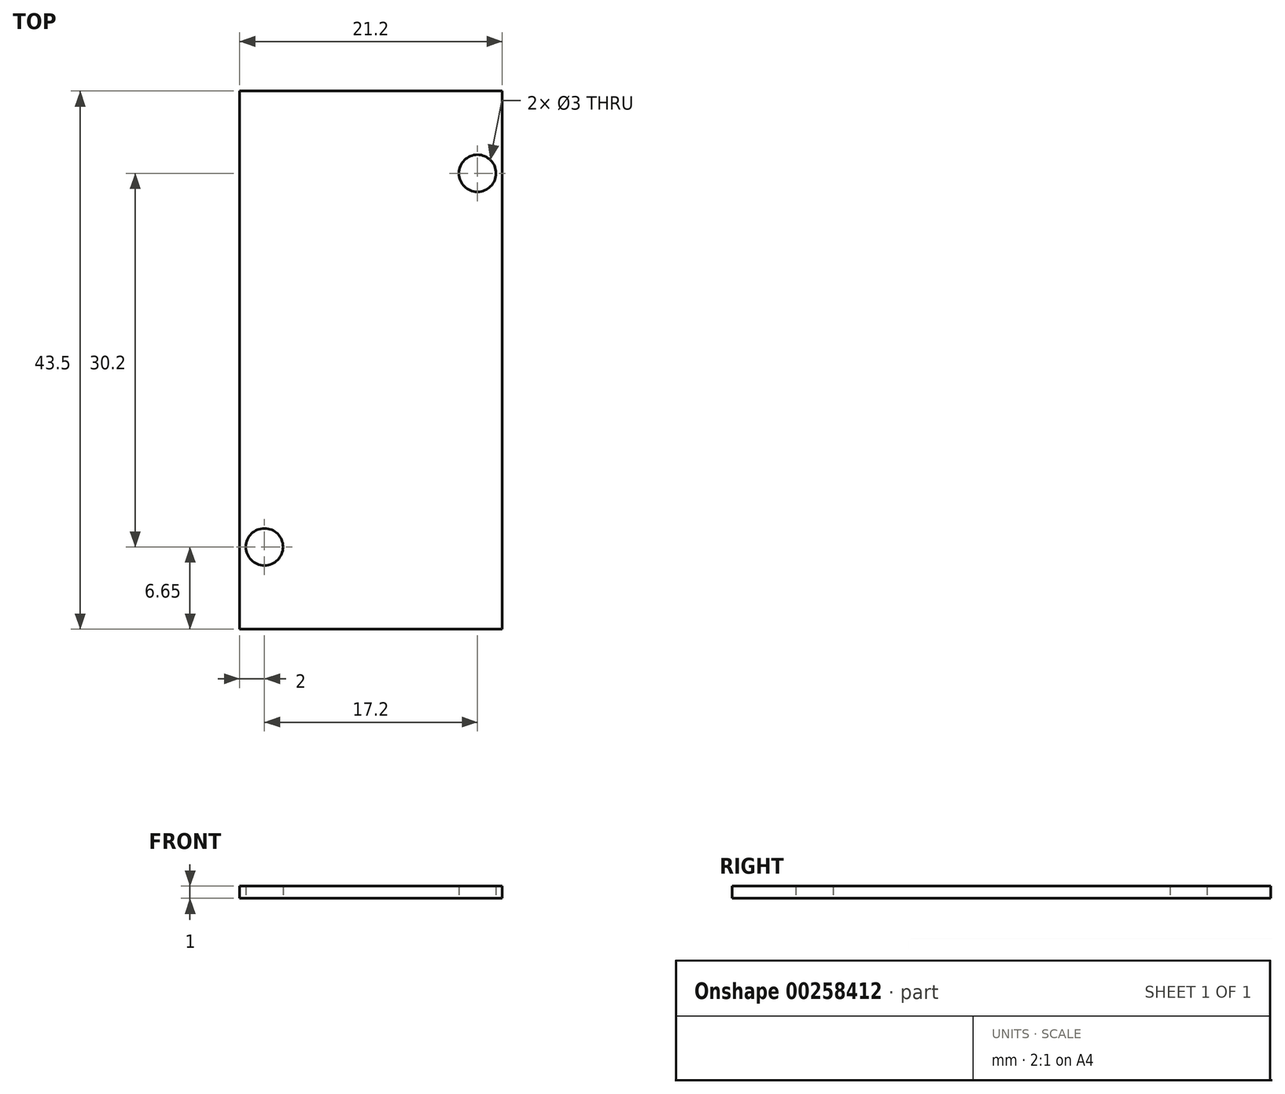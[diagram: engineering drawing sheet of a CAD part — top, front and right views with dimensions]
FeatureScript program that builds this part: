
annotation { "Feature Type Name" : "Feature", "Feature Type Description" : "" }
export const myFeature = defineFeature(function(context is Context, id is Id, definition is map)
    precondition{}
    {
        {
            var Q0;
            Q0=qCreatedBy(makeId("Top.planeOp"),FACE);
            var sketch = newSketch(context, id + "F0", { "sketchPlane" : qUnion([Q0])});
            skLineSegment(sketch, "E0.bottom", {"start": v(10.6, -21.75) * mm, "end": v(-10.6, -21.75) * mm});
            skLineSegment(sketch, "E0.top", {"start": v(10.6, 21.75) * mm, "end": v(-10.6, 21.75) * mm});
            skLineSegment(sketch, "E0.left", {"start": v(10.6, -21.75) * mm, "end": v(10.6, 21.75) * mm});
            skLineSegment(sketch, "E0.right", {"start": v(-10.6, -21.75) * mm, "end": v(-10.6, 21.75) * mm});
            skPoint(sketch, "E0.middle", {"position": v(0, 0) * mm});
            skCircle(sketch, "E1", {"center": v(8.6, 15.1) * mm, "radius": 1.5 * mm});
            skCircle(sketch, "E2.MirrorC", {"center": v(-8.6, -15.1) * mm, "radius": 1.5 * mm});
            skSolve(sketch);
        }
        {
            var Q0;
            Q0=makeQuery(id+"F0.imprint","IMPRINT",FACE,{"disambiguationData":[TD([[makeQuery(id+"F0.imprint","IMPRINT",EDGE,{"derivedFrom":sQuery(id+"F0.wireOp",EDGE,"E0.bottom")}),-1.0]])]});
            extrude(context, id + "F1", {"entities" : qUnion([Q0]), "depth" : 1 * mm});
        }
    });
